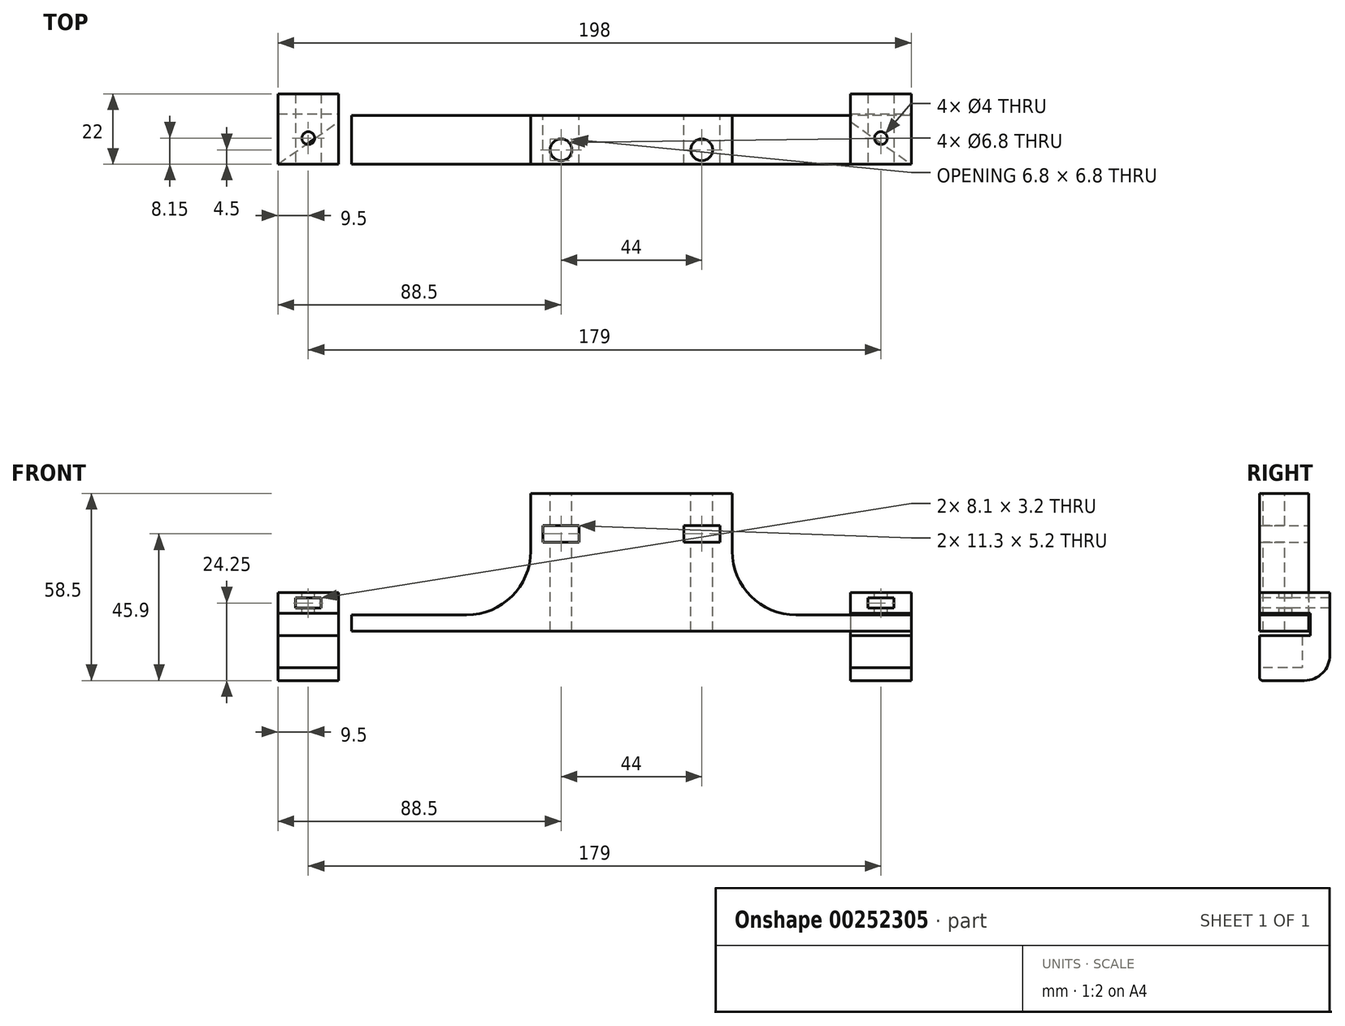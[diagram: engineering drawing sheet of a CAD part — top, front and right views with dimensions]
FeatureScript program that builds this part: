
annotation { "Feature Type Name" : "Feature", "Feature Type Description" : "" }
export const myFeature = defineFeature(function(context is Context, id is Id, definition is map)
    precondition{}
    {
        {
            var Q0;
            Q0=qCreatedBy(makeId("Front.planeOp"),FACE);
            var sketch = newSketch(context, id + "F0", { "sketchPlane" : qUnion([Q0])});
            skLineSegment(sketch, "E0.bottom", {"start": v(-87.5, 0) * mm, "end": v(87.5, 0) * mm});
            skLineSegment(sketch, "E0.top", {"start": v(-31.5, 43) * mm, "end": v(31.5, 43) * mm});
            skLineSegment(sketch, "E0.left", {"start": v(-87.5, 0) * mm, "end": v(-87.5, 5) * mm});
            skLineSegment(sketch, "E0.right", {"start": v(87.5, 0) * mm, "end": v(87.5, 5) * mm});
            skLineSegment(sketch, "E1.top", {"start": v(-87.5, 5) * mm, "end": v(-31.5, 5) * mm});
            skLineSegment(sketch, "E1.right", {"start": v(-31.5, 43) * mm, "end": v(-31.5, 5) * mm});
            skLineSegment(sketch, "E2.top", {"start": v(87.5, 5) * mm, "end": v(31.5, 5) * mm});
            skLineSegment(sketch, "E2.right", {"start": v(31.5, 43) * mm, "end": v(31.5, 5) * mm});
            skPoint(sketch, "E3", {"position": v(0, 43) * mm});
            skLineSegment(sketch, "E4.bottom", {"start": v(-16.35, 27.8) * mm, "end": v(-27.65, 27.8) * mm});
            skLineSegment(sketch, "E4.top", {"start": v(-16.35, 33) * mm, "end": v(-27.65, 33) * mm});
            skLineSegment(sketch, "E4.left", {"start": v(-16.35, 27.8) * mm, "end": v(-16.35, 33) * mm});
            skLineSegment(sketch, "E4.right", {"start": v(-27.65, 27.8) * mm, "end": v(-27.65, 33) * mm});
            skPoint(sketch, "E4.middle", {"position": v(-22, 30.4) * mm});
            skLineSegment(sketch, "E5", {"start": v(0, 75.27) * mm, "end": v(0, -41.68) * mm, "construction": true});
            skLineSegment(sketch, "E6.MirrorCS", {"start": v(16.35, 27.8) * mm, "end": v(27.65, 27.8) * mm});
            skLineSegment(sketch, "E7.MirrorCS", {"start": v(16.35, 33) * mm, "end": v(27.65, 33) * mm});
            skLineSegment(sketch, "E8.MirrorCS", {"start": v(16.35, 27.8) * mm, "end": v(16.35, 33) * mm});
            skLineSegment(sketch, "E9.MirrorCS", {"start": v(27.65, 27.8) * mm, "end": v(27.65, 33) * mm});
            skPoint(sketch, "E10.MirrorP", {"position": v(22, 30.4) * mm});
            skSolve(sketch);
        }
        {
            var Q0;
            Q0 = qSketchRegion(id + "F0", true);
            extrude(context, id + "F1", {"entities" : qUnion([Q0]), "depth" : 15.3 * mm});
        }
        {
            var Q0;
            Q0=makeQuery(id+"F1.opExtrude","SWEPT_FACE",FACE,{"disambiguationData":[OSD([sQuery(id+"F0.wireOp",EDGE,"E0.top")])]});
            var sketch = newSketch(context, id + "F2", { "sketchPlane" : qUnion([Q0])});
            skCircle(sketch, "E11", {"center": v(-22, -10.8) * mm, "radius": 3.4 * mm});
            skPoint(sketch, "E11.centerSnap0", {"position": v(-31.5, -7.65) * mm});
            skLineSegment(sketch, "E12", {"start": v(0, 39.19) * mm, "end": v(0, -33.71) * mm, "construction": true});
            skCircle(sketch, "E13.MirrorC", {"center": v(22, -10.8) * mm, "radius": 3.4 * mm});
            skSolve(sketch);
        }
        {
            var Q0;
            Q0 = qSketchRegion(id + "F2", true);
            var Q1;
            Q1=makeQuery(id+"F1.opExtrude","SWEPT_FACE",FACE,{"disambiguationData":[OSD([sQuery(id+"F0.wireOp",EDGE,"E0.bottom")])]});
            extrude(context, id + "F3", {"entities" : qUnion([Q0]), "operationType" : NewBodyOperationType.REMOVE, "endBound" : BoundingType.UP_TO_SURFACE, "oppositeDirection" : true, "endBoundEntityFace" : qUnion([Q1]), "depth" : 25 * mm});
        }
        {
            var Q0;
            Q0=makeQuery(id+"F1.opExtrude","SWEPT_FACE",FACE,{"disambiguationData":[OSD([sQuery(id+"F0.wireOp",EDGE,"E0.right")])]});
            var sketch = newSketch(context, id + "F4", { "sketchPlane" : qUnion([Q0])});
            skLineSegment(sketch, "E14.bottom", {"start": v(-15.3, 12) * mm, "end": v(6.7, 12) * mm});
            skLineSegment(sketch, "E14.top", {"start": v(-15.3, 5.5) * mm, "end": v(0.5, 5.5) * mm});
            skLineSegment(sketch, "E14.left", {"start": v(-15.3, 12) * mm, "end": v(-15.3, 5.5) * mm});
            skLineSegment(sketch, "E15.right", {"start": v(0.5, 5.5) * mm, "end": v(0.5, -11.5) * mm});
            skLineSegment(sketch, "E16.top", {"start": v(0.5, -11.5) * mm, "end": v(-15.3, -11.5) * mm});
            skLineSegment(sketch, "E16.right", {"start": v(-15.3, -14.5) * mm, "end": v(-15.3, -11.5) * mm});
            skLineSegment(sketch, "E17", {"start": v(-14.3, -15.5) * mm, "end": v(-1.3, -15.5) * mm});
            skLineSegment(sketch, "E18", {"start": v(6.7, 12) * mm, "end": v(6.7, -7.5) * mm});
            skPoint(sketch, "E19.visualSharp", {"position": v(-15.3, -11.5) * mm});
            skLineSegment(sketch, "E19.filletArc", {"start": v(-15.3, -11.5) * mm, "end": v(-15.3, -11.5) * mm});
            skPoint(sketch, "E20.visualSharp", {"position": v(-15.3, -15.5) * mm});
            skArc(sketch, "E20.filletArc", {"start": v(-15.3, -14.5) * mm, "mid": v(-15, -15.2) * mm, "end": v(-14.3, -15.5) * mm});
            skPoint(sketch, "E21.visualSharp", {"position": v(6.7, -15.5) * mm});
            skArc(sketch, "E21.filletArc", {"start": v(-1.3, -15.5) * mm, "mid": v(4.36, -13.16) * mm, "end": v(6.7, -7.5) * mm});
            skSolve(sketch);
        }
        {
            var Q0;
            Q0 = qSketchRegion(id + "F4", true);
            extrude(context, id + "F5", {"entities" : qUnion([Q0]), "oppositeDirection" : true, "depth" : 19 * mm});
        }
        {
            var Q0;
            Q0=makeQuery(id+"F5.opExtrude","SWEPT_FACE",FACE,{"disambiguationData":[OSD([sQuery(id+"F4.wireOp",EDGE,"E14.left")])]});
            var sketch = newSketch(context, id + "F6", { "sketchPlane" : qUnion([Q0])});
            skLineSegment(sketch, "E22.bottom", {"start": v(82.05, 7.15) * mm, "end": v(73.95, 7.15) * mm});
            skLineSegment(sketch, "E22.top", {"start": v(82.05, 10.35) * mm, "end": v(73.95, 10.35) * mm});
            skLineSegment(sketch, "E22.left", {"start": v(82.05, 7.15) * mm, "end": v(82.05, 10.35) * mm});
            skLineSegment(sketch, "E22.right", {"start": v(73.95, 7.15) * mm, "end": v(73.95, 10.35) * mm});
            skPoint(sketch, "E22.middle", {"position": v(78, 8.75) * mm});
            skPoint(sketch, "E22.middle.positionSnap0", {"position": v(78, 12) * mm});
            skPoint(sketch, "E22.middle.positionSnap1", {"position": v(87.5, 8.75) * mm});
            skPoint(sketch, "E22.centerSnap0", {"position": v(78, 12) * mm});
            skPoint(sketch, "E22.centerSnap1", {"position": v(87.5, 8.75) * mm});
            skSolve(sketch);
        }
        {
            var Q0;
            Q0 = qSketchRegion(id + "F6", true);
            var Q1;
            Q1=makeQuery(id+"F5.opExtrude","SWEPT_FACE",FACE,{"disambiguationData":[OSD([sQuery(id+"F4.wireOp",EDGE,"E18")])]});
            extrude(context, id + "F7", {"entities" : qUnion([Q0]), "operationType" : NewBodyOperationType.REMOVE, "endBound" : BoundingType.UP_TO_SURFACE, "oppositeDirection" : true, "endBoundEntityFace" : qUnion([Q1]), "depth" : 25 * mm});
        }
        {
            var Q0;
            Q0=makeQuery(id+"F5.opExtrude","SWEPT_FACE",FACE,{"disambiguationData":[OSD([sQuery(id+"F4.wireOp",EDGE,"E14.bottom")])]});
            var sketch = newSketch(context, id + "F8", { "sketchPlane" : qUnion([Q0])});
            skCircle(sketch, "E23", {"center": v(78, -7.15) * mm, "radius": 2 * mm});
            skPoint(sketch, "E23.centerSnap0", {"position": v(78, 6.7) * mm});
            skPoint(sketch, "E23.centerSnap1", {"position": v(68.5, -4.3) * mm});
            skSolve(sketch);
        }
        {
            var Q0;
            Q0 = qSketchRegion(id + "F8", true);
            var Q1;
            Q1=makeQuery(id+"F5.opExtrude","SWEPT_FACE",FACE,{"disambiguationData":[OSD([sQuery(id+"F4.wireOp",EDGE,"E14.top")])]});
            extrude(context, id + "F9", {"entities" : qUnion([Q0]), "operationType" : NewBodyOperationType.REMOVE, "endBound" : BoundingType.UP_TO_SURFACE, "oppositeDirection" : true, "endBoundEntityFace" : qUnion([Q1]), "depth" : 25 * mm});
        }
        {
            var Q0;
            Q0=makeQuery(id+"F5.opExtrude","SWEPT_BODY",BODY,{"disambiguationData":[OSD([sQuery(id+"F4.wireOp",EDGE,"E14.bottom"),sQuery(id+"F4.wireOp",EDGE,"E14.top"),sQuery(id+"F4.wireOp",EDGE,"E14.left"),sQuery(id+"F4.wireOp",EDGE,"E15.right"),sQuery(id+"F4.wireOp",EDGE,"E16.top"),sQuery(id+"F4.wireOp",EDGE,"E17"),sQuery(id+"F4.wireOp",EDGE,"E18"),sQuery(id+"F4.wireOp",EDGE,"E19.filletArc"),sQuery(id+"F4.wireOp",EDGE,"E20.filletArc"),sQuery(id+"F4.wireOp",EDGE,"E21.filletArc")])]});
            transform(context, id + "F10", {"entities" : qUnion([Q0]), "transformType" : TransformType.TRANSLATION_3D, "dx" : -179 * mm, "dy" : 0 * mm, "dz" : 0 * mm, "makeCopy" : true});
        }
        {
            var Q0;
            Q0=makeQuery(id+"F5.opExtrude","SWEPT_FACE",FACE,{"disambiguationData":[OSD([sQuery(id+"F4.wireOp",EDGE,"E16.top")])]});
            var sketch = newSketch(context, id + "F11", { "sketchPlane" : qUnion([Q0])});
            skLineSegment(sketch, "E24", {"start": v(68.5, 0.5) * mm, "end": v(87.5, 0.5) * mm});
            skLineSegment(sketch, "E25", {"start": v(68.5, 0.5) * mm, "end": v(68.5, -2) * mm});
            skLineSegment(sketch, "E26", {"start": v(68.5, -2) * mm, "end": v(87.5, -15.3) * mm});
            skLineSegment(sketch, "E27", {"start": v(87.5, 0.5) * mm, "end": v(87.5, -15.3) * mm});
            skSolve(sketch);
        }
        {
            var Q0;
            Q0 = qSketchRegion(id + "F11", true);
            extrude(context, id + "F12", {"entities" : qUnion([Q0]), "operationType" : NewBodyOperationType.ADD, "depth" : 10 * mm});
        }
        {
            var Q0;
            Q0=makeQuery(id+"F10.opPattern","COPY",FACE,{"derivedFrom":makeQuery(id+"F5.opExtrude","SWEPT_FACE",FACE,{"disambiguationData":[OSD([sQuery(id+"F4.wireOp",EDGE,"E16.top")])]}),"instanceName":"1"});
            var sketch = newSketch(context, id + "F13", { "sketchPlane" : qUnion([Q0])});
            skLineSegment(sketch, "E28", {"start": v(-91.5, 0.5) * mm, "end": v(-110.5, 0.5) * mm});
            skLineSegment(sketch, "E29", {"start": v(-91.5, 0.5) * mm, "end": v(-91.5, -2) * mm});
            skLineSegment(sketch, "E30", {"start": v(-110.5, 0.5) * mm, "end": v(-110.5, -15.3) * mm});
            skLineSegment(sketch, "E31", {"start": v(-110.5, -15.3) * mm, "end": v(-91.5, -2) * mm});
            skSolve(sketch);
        }
        {
            var Q0;
            Q0 = qSketchRegion(id + "F13", true);
            extrude(context, id + "F14", {"entities" : qUnion([Q0]), "operationType" : NewBodyOperationType.ADD, "depth" : 10 * mm});
        }
        {
            var Q0;
            Q0=makeQuery(id+"F1.opExtrude","SWEPT_EDGE",EDGE,{"disambiguationData":[OSD([sQuery(id+"F0.wireOp",EDGE,"E2.top"),sQuery(id+"F0.wireOp",EDGE,"E2.right")])]});
            var Q1;
            Q1=makeQuery(id+"F1.opExtrude","SWEPT_EDGE",EDGE,{"disambiguationData":[OSD([sQuery(id+"F0.wireOp",EDGE,"E1.top"),sQuery(id+"F0.wireOp",EDGE,"E1.right")])]});
            fillet(context, id + "F15", {"entities" : qUnion([Q0, Q1]), "radius" : 20 * mm, "tangentPropagation" : true, "allowEdgeOverflow" : false});
        }
    });
